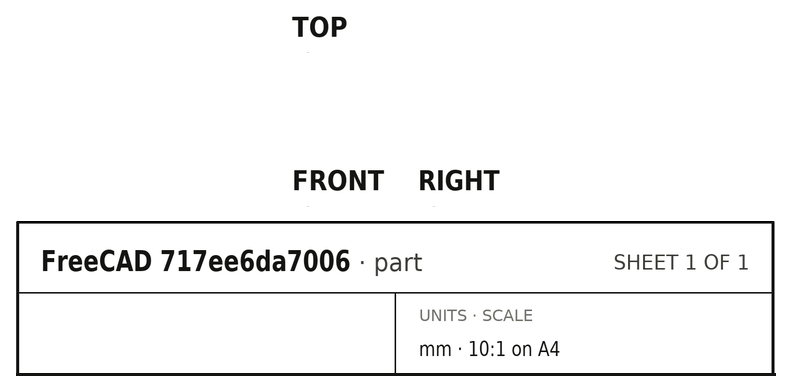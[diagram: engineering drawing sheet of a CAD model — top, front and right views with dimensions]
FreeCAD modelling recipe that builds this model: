
FCSTD DOCUMENT  (FreeCAD 0.21R33694 (Git))
Label: diffPair
License: All rights reserved
LicenseURL: http://en.wikipedia.org/wiki/All_rights_reserved
objects: Part::Part2DObjectPython×22, App::FeaturePython×10, Part::Extrusion×4, Part::Cut×2, Part::FeaturePython×2
note: 30 computed .brp shape members not serialized (recipe doc carries the construction recipe); baked Part::Feature solids carry a one-line shape summary decoded from their .brp

FEATURE [Part::Part2DObjectPython] Wire  # Draft 2D object (typed FeaturePython)
  Area = 0.0014181
  ChamferSize = 0
  Closed = true
  End = (-0.05,0,0)
  FilletRadius = 0
  Length = 0.221006
  MakeFace = true
  Placement = pos=(-0.15,0,0) rot=(0,0,1;0rad)
  Points = (4) [(0,0,0),(0.00545955,0.015,0),(0.0945402,0.015,0),(0.1,-6.12323e-18,0)]
  Start = (-0.15,0,0)
  Subdivisions = 0
FEATURE [Part::Part2DObjectPython] Wire001  # Draft 2D object (typed FeaturePython)
  Area = 0.0014181
  ChamferSize = 0
  Closed = true
  End = (0.15,0,0)
  FilletRadius = 0
  Length = 0.221006
  MakeFace = true
  Placement = pos=(0.05,0,0) rot=(0,0,1;0rad)
  Points = (4) [(0,0,0),(0.00545955,0.015,0),(0.0945402,0.015,0),(0.1,-6.12323e-18,0)]
  Start = (0.05,0,0)
  Subdivisions = 0
FEATURE [Part::Part2DObjectPython] Rectangle  # Draft 2D object (typed FeaturePython)
  Area = 0.13
  ChamferSize = 0
  Columns = 1
  FilletRadius = 0
  Height = 0.1
  Length = 1.3
  MakeFace = true
  Placement = pos=(-0.65,-0.1,0) rot=(0,0,1;0rad)
  Rows = 1
FEATURE [Part::Part2DObjectPython] Rectangle001  # Draft 2D object (typed FeaturePython)
  Area = 0.13
  ChamferSize = 0
  Columns = 1
  FilletRadius = 0
  Height = 0.1
  Length = 1.3
  MakeFace = true
  Placement = pos=(-0.65,0,0) rot=(0,0,1;0rad)
  Rows = 1
FEATURE [Part::Part2DObjectPython] Clone2D  label="Wire (2D)"  # Draft 2D object (typed FeaturePython)
  Fuse = false
  Objects = -> [Wire]
  Placement = pos=(-0.15,0,0) rot=(0,0,1;0rad)
  Scale = (1,1,1)
FEATURE [Part::Part2DObjectPython] Clone2D001  label="Wire001 (2D)"  # Draft 2D object (typed FeaturePython)
  Fuse = false
  Objects = -> [Wire001]
  Placement = pos=(0.05,0,0) rot=(0,0,1;0rad)
  Scale = (1,1,1)
FEATURE [Part::Part2DObjectPython] Clone2D002  label="Rectangle (2D)"  # Draft 2D object (typed FeaturePython)
  Fuse = false
  Objects = -> [Rectangle]
  Placement = pos=(-0.65,-0.1,0) rot=(0,0,1;0rad)
  Scale = (1,1,1)
FEATURE [Part::Part2DObjectPython] Clone2D003  label="Rectangle001 (2D)"  # Draft 2D object (typed FeaturePython)
  Fuse = false
  Objects = -> [Rectangle001]
  Placement = pos=(-0.65,0,0) rot=(0,0,1;0rad)
  Scale = (1,1,1)
FEATURE [Part::Part2DObjectPython] Clone2D004  label="Wire (2D)001"  # Draft 2D object (typed FeaturePython)
  Fuse = false
  Objects = -> [Wire]
  Placement = pos=(-0.15,0,0) rot=(0,0,1;0rad)
  Scale = (1,1,1)
FEATURE [Part::Part2DObjectPython] Clone2D005  label="Wire001 (2D)001"  # Draft 2D object (typed FeaturePython)
  Fuse = false
  Objects = -> [Wire001]
  Placement = pos=(0.05,0,0) rot=(0,0,1;0rad)
  Scale = (1,1,1)
FEATURE [Part::Part2DObjectPython] Clone2D006  label="Rectangle (2D)001"  # Draft 2D object (typed FeaturePython)
  Fuse = false
  Objects = -> [Rectangle]
  Placement = pos=(-0.65,-0.1,0) rot=(0,0,1;0rad)
  Scale = (1,1,1)
FEATURE [Part::Part2DObjectPython] Clone2D007  label="Rectangle001 (2D)001"  # Draft 2D object (typed FeaturePython)
  Fuse = false
  Objects = -> [Rectangle001]
  Placement = pos=(-0.65,0,0) rot=(0,0,1;0rad)
  Scale = (1,1,1)
FEATURE [Part::Extrusion] Extrude004
  Base = -> Clone2D
  Dir = (0,0,1)
  DirMode = 2
  FaceMakerClass = Part::FaceMakerBullseye
  LengthFwd = 2
  LengthRev = 0
  Solid = false
  Symmetric = false
FEATURE [Part::Extrusion] Extrude005
  Base = -> Clone2D001
  Dir = (0,0,1)
  DirMode = 2
  FaceMakerClass = Part::FaceMakerBullseye
  LengthFwd = 2
  LengthRev = 0
  Solid = false
  Symmetric = false
FEATURE [Part::Extrusion] Extrude006
  Base = -> Clone2D002
  Dir = (0,0,1)
  DirMode = 2
  FaceMakerClass = Part::FaceMakerBullseye
  LengthFwd = 2
  LengthRev = 0
  Solid = false
  Symmetric = false
FEATURE [Part::Extrusion] Extrude007
  Base = -> Clone2D003
  Dir = (0,0,1)
  DirMode = 2
  FaceMakerClass = Part::FaceMakerBullseye
  LengthFwd = 2
  LengthRev = 0
  Solid = false
  Symmetric = false
FEATURE [Part::Cut] Cut002
  Base = -> Extrude007
  Tool = -> Extrude004
FEATURE [Part::Cut] Cut003
  Base = -> Cut002
  Tool = -> Extrude005
FEATURE [App::FeaturePython] Text010  label="_Sin(PV){port1}"  # WARN: FeaturePython — macro-defined, semantics opaque (R4)
  Placement = pos=(5.00075,-5.09743,10) rot=(0,0,1;0rad)
  Text = .
FEATURE [App::FeaturePython] Text011  label="_Sout(PV){port2}"  # WARN: FeaturePython — macro-defined, semantics opaque (R4)
  Placement = pos=(5.00075,-5.09743,10) rot=(0,0,1;0rad)
  Text = .
FEATURE [App::FeaturePython] Text012  label="_Lin(1,voltage,in1){v11}"  # WARN: FeaturePython — macro-defined, semantics opaque (R4)
  Placement = pos=(5.00075,-5.09743,10) rot=(0,0,1;0rad)
  Text = .
FEATURE [App::FeaturePython] Text013  label="_Lin(1,current,in1){i11}"  # WARN: FeaturePython — macro-defined, semantics opaque (R4)
  Placement = pos=(5.00075,-5.09743,10) rot=(0,0,1;0rad)
  Text = .
FEATURE [App::FeaturePython] Text014  label="_Lin(2,voltage,in2){v12}"  # WARN: FeaturePython — macro-defined, semantics opaque (R4)
  Placement = pos=(5.00075,-5.09743,10) rot=(0,0,1;0rad)
  Text = .
FEATURE [App::FeaturePython] Text015  label="_Lin(2,current,in2){i12}"  # WARN: FeaturePython — macro-defined, semantics opaque (R4)
  Placement = pos=(5.00075,-5.09743,10) rot=(0,0,1;0rad)
  Text = .
FEATURE [App::FeaturePython] Text016  label="_Lout(3,voltage,out3){v21}"  # WARN: FeaturePython — macro-defined, semantics opaque (R4)
  Placement = pos=(5.00075,-5.09743,10) rot=(0,0,1;0rad)
  Text = .
FEATURE [App::FeaturePython] Text017  label="_Lout(3,current,out3){i21}"  # WARN: FeaturePython — macro-defined, semantics opaque (R4)
  Placement = pos=(5.00075,-5.09743,10) rot=(0,0,1;0rad)
  Text = .
FEATURE [App::FeaturePython] Text018  label="_Lout(4,voltage,out4){v22}"  # WARN: FeaturePython — macro-defined, semantics opaque (R4)
  Placement = pos=(5.00075,-5.09743,10) rot=(0,0,1;0rad)
  Text = .
FEATURE [App::FeaturePython] Text019  label="_Lout(4,current,out4){i22}"  # WARN: FeaturePython — macro-defined, semantics opaque (R4)
  Placement = pos=(5.00075,-5.09743,10) rot=(0,0,1;0rad)
  Text = .
FEATURE [Part::Part2DObjectPython] Wire006  label="_Pi22"  # Draft 2D object (typed FeaturePython)
  Area = 1.4181e-09
  ChamferSize = 0
  Closed = true
  End = (5e-05,-0.0999,4.995)
  FilletRadius = 0
  Length = 0.000221006
  MakeFace = true
  Placement = pos=(0.00015,-0.0999,4.995) rot=(0.707107,0.707107,0;3.14159rad)
  Points = (4) [(0,0,0),(1.5e-05,-5.45983e-06,0),(1.5e-05,-9.45404e-05,0),(0,-0.0001,0)]
  Start = (0.00015,-0.0999,4.995)
  Subdivisions = 0
FEATURE [Part::Part2DObjectPython] Wire007  label="_Pi21"  # Draft 2D object (typed FeaturePython)
  Area = 1.4181e-09
  ChamferSize = 0
  Closed = true
  End = (-0.00015,-0.0999,4.995)
  FilletRadius = 0
  Length = 0.000221006
  MakeFace = true
  Placement = pos=(-5e-05,-0.0999,4.995) rot=(0.707107,0.707107,0;3.14159rad)
  Points = (4) [(0,0,0),(1.5e-05,-5.45983e-06,0),(1.5e-05,-9.45404e-05,0),(0,-0.0001,0)]
  Start = (-5e-05,-0.0999,4.995)
  Subdivisions = 0
FEATURE [Part::Part2DObjectPython] Wire008  label="_Pi11"  # Draft 2D object (typed FeaturePython)
  Area = 1.4181e-09
  ChamferSize = 0
  Closed = true
  End = (-5e-05,-0.0999,4.997)
  FilletRadius = 0
  Length = 0.000221006
  MakeFace = true
  Placement = pos=(-0.00015,-0.0999,4.997) rot=(0,0,1;0rad)
  Points = (4) [(0,0,0),(5.45955e-06,1.5e-05,0),(9.45402e-05,1.5e-05,0),(0.0001,0,0)]
  Start = (-0.00015,-0.0999,4.997)
  Subdivisions = 0
FEATURE [Part::Part2DObjectPython] Wire009  label="_Pi12"  # Draft 2D object (typed FeaturePython)
  Area = 1.4181e-09
  ChamferSize = 0
  Closed = true
  End = (0.00015,-0.0999,4.997)
  FilletRadius = 0
  Length = 0.000221006
  MakeFace = true
  Placement = pos=(5e-05,-0.0999,4.997) rot=(0,0,1;0rad)
  Points = (4) [(0,0,0),(5.45955e-06,1.5e-05,0),(9.45402e-05,1.5e-05,0),(0.0001,0,0)]
  Start = (5e-05,-0.0999,4.997)
  Subdivisions = 0
FEATURE [Part::Part2DObjectPython] Rectangle013  label="_Pport1"  # Draft 2D object (typed FeaturePython)
  Area = 2.6e-07
  ChamferSize = 0
  Columns = 1
  FilletRadius = 0
  Height = 0.0002
  Length = 0.0013
  MakeFace = true
  Placement = pos=(-0.00065,-0.1,4.997) rot=(0,0,1;0rad)
  Rows = 1
FEATURE [Part::Part2DObjectPython] Line  label="_Pv11"  # Draft 2D object (typed FeaturePython)
  Area = 0
  ChamferSize = 0
  Closed = false
  End = (-0.0001,-0.0999,4.997)
  FilletRadius = 0
  Length = 0.0001
  MakeFace = true
  Placement = pos=(0,-0.1,4.997) rot=(0,0,1;0rad)
  Points = (2) [(-0.0001,0,0),(-0.0001,0.0001,0)]
  Start = (-0.0001,-0.1,4.997)
  Subdivisions = 0
FEATURE [Part::Part2DObjectPython] Line004  label="_Pv12"  # Draft 2D object (typed FeaturePython)
  Area = 0
  ChamferSize = 0
  Closed = false
  End = (0.0001,-0.0999,4.997)
  FilletRadius = 0
  Length = 0.0001
  MakeFace = true
  Placement = pos=(0,-0.1,4.997) rot=(0,0,1;0rad)
  Points = (2) [(0.0001,0,0),(0.0001,0.0001,0)]
  Start = (0.0001,-0.1,4.997)
  Subdivisions = 0
FEATURE [Part::Part2DObjectPython] Rectangle014  label="_Pport2"  # Draft 2D object (typed FeaturePython)
  Area = 2.6e-07
  ChamferSize = 0
  Columns = 1
  FilletRadius = 0
  Height = 0.0013
  Length = 0.0002
  MakeFace = true
  Placement = pos=(-0.00065,-0.1,4.995) rot=(0.707107,0.707107,0;3.14159rad)
  Rows = 1
FEATURE [Part::Part2DObjectPython] Line005  label="_Pv21"  # Draft 2D object (typed FeaturePython)
  Area = 0
  ChamferSize = 0
  Closed = false
  End = (-0.0001,-0.0999,4.995)
  FilletRadius = 0
  Length = 0.0001
  MakeFace = true
  Placement = pos=(0,-0.1,4.995) rot=(0.707107,0.707107,0;3.14159rad)
  Points = (2) [(1.38778e-17,-0.0001,0),(0.0001,-0.0001,0)]
  Start = (-0.0001,-0.1,4.995)
  Subdivisions = 0
FEATURE [Part::Part2DObjectPython] Line006  label="_Pv22"  # Draft 2D object (typed FeaturePython)
  Area = 0
  ChamferSize = 0
  Closed = false
  End = (0.0001,-0.0999,4.995)
  FilletRadius = 0
  Length = 0.0001
  MakeFace = true
  Placement = pos=(0,-0.1,4.995) rot=(0.707107,0.707107,0;3.14159rad)
  Points = (2) [(1.38778e-17,0.0001,0),(0.0001,0.0001,0)]
  Start = (0.0001,-0.1,4.995)
  Subdivisions = 0
FEATURE [Part::FeaturePython] BooleanFragments  # WARN: FeaturePython — macro-defined, semantics opaque (R4)
  Mode = 0
  Objects = -> [Extrude006,Cut003]
  Tolerance = 0
FEATURE [Part::FeaturePython] Clone  label="scaled"  # Draft clone (typed FeaturePython)
  AttacherType = Attacher::AttachEngine3D
  Fuse = false
  Objects = -> [BooleanFragments]
  Placement = pos=(0,-0.0999,4.995) rot=(0,0,1;0rad)
  Scale = (0.001,0.001,0.001)
